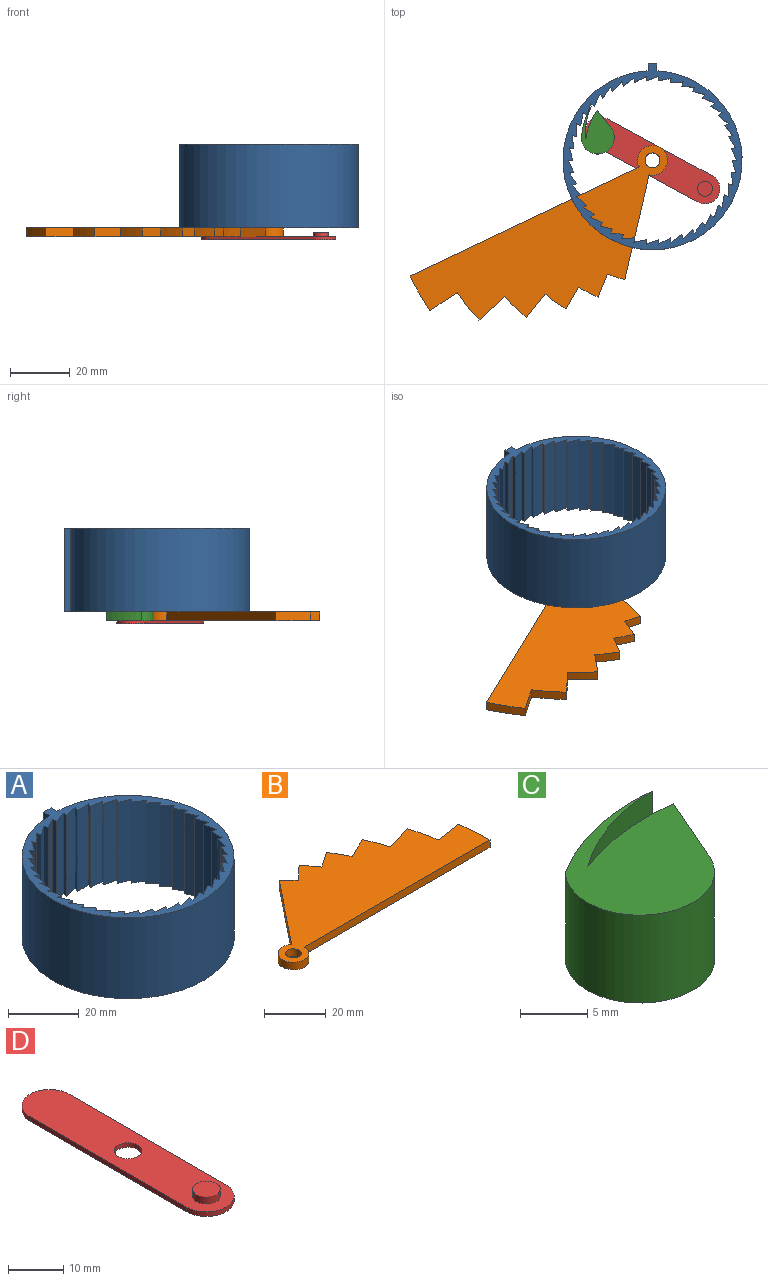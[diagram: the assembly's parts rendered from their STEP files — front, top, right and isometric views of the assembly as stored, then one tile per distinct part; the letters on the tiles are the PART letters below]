
ASSEMBLY  parts=4 mates=3
PART A: 90 faces, bbox 60x62.3x28 mm
  f0: plane 28x2.3mm, normal (-1,0,0), area 64.4mm2, adj f1,f87,f88,f89
  f1: cylinder r=30mm len=60mm, axis (0,0,-1), area 5193.8mm2, adj f0,f2,f88,f89
  f2: plane 28x2.3mm, normal (1,0,0), area 64.4mm2, adj f1,f87,f88,f89
  f3: plane 28x3.98mm, normal (-0.91,-0.41,0), area 122.2mm2, adj f4,f86,f88,f89
  f4: plane 28x1.5mm, normal (0,1,0), area 42mm2, adj f3,f5,f88,f89
  f5: plane 28x4.2mm, normal (-0.96,-0.27,0), area 122.2mm2, adj f4,f6,f88,f89
  f6: plane 28x1.48mm, normal (0.15,0.99,0), area 42mm2, adj f5,f7,f88,f89
  f7: plane 28x4.33mm, normal (-0.99,-0.13,0), area 122.2mm2, adj f6,f8,f88,f89
  f8: plane 28x1.43mm, normal (0.29,0.96,0), area 42mm2, adj f7,f9,f88,f89
  f9: plane 28x4.36mm, normal (-1,0.02,0), area 122.2mm2, adj f8,f10,f88,f89
  f10: plane 28x1.35mm, normal (0.43,0.9,0), area 42mm2, adj f9,f11,f88,f89
  f11: plane 28x4.3mm, normal (-0.98,0.17,0), area 122.2mm2, adj f10,f12,f88,f89
  f12: plane 28x1.24mm, normal (0.56,0.83,0), area 42mm2, adj f11,f13,f88,f89
  f13: plane 28x4.14mm, normal (-0.95,0.32,0), area 122.2mm2, adj f12,f14,f88,f89
  f14: plane 28x1.1mm, normal (0.68,0.73,0), area 42mm2, adj f13,f15,f88,f89
  f15: plane 28x3.89mm, normal (-0.89,0.46,0), area 122.2mm2, adj f14,f16,f88,f89
  f16: plane 28x1.17mm, normal (0.78,0.62,0), area 42mm2, adj f15,f17,f88,f89
  f17: plane 28x3.55mm, normal (-0.81,0.58,0), area 122.2mm2, adj f16,f18,f88,f89
  f18: plane 28x1.3mm, normal (0.87,0.5,0), area 42mm2, adj f17,f19,f88,f89
  f19: plane 28x3.13mm, normal (-0.72,0.7,0), area 122.2mm2, adj f18,f20,f88,f89
  f20: plane 28x1.4mm, normal (0.93,0.37,0), area 42mm2, adj f19,f21,f88,f89
  f21: plane 28x3.48mm, normal (-0.6,0.8,0), area 122.2mm2, adj f20,f22,f88,f89
  f22: plane 28x1.46mm, normal (0.97,0.22,0), area 42mm2, adj f21,f23,f88,f89
  f23: plane 28x3.83mm, normal (-0.48,0.88,0), area 122.2mm2, adj f22,f24,f88,f89
  f24: plane 28x1.5mm, normal (1,0.07,0), area 42mm2, adj f23,f25,f88,f89
  f25: plane 28x4.1mm, normal (-0.34,0.94,0), area 122.2mm2, adj f24,f26,f88,f89
  f26: plane 28x1.5mm, normal (1,-0.07,0), area 42mm2, adj f25,f27,f88,f89
  f27: plane 28x4.28mm, normal (-0.2,0.98,0), area 122.2mm2, adj f26,f28,f88,f89
  f28: plane 28x1.46mm, normal (0.97,-0.22,0), area 42mm2, adj f27,f29,f88,f89
  f29: plane 28x4.36mm, normal (-0.05,1,0), area 122.2mm2, adj f28,f30,f88,f89
  f30: plane 28x1.4mm, normal (0.93,-0.37,0), area 42mm2, adj f29,f31,f88,f89
  f31: plane 28x4.34mm, normal (0.1,1,0), area 122.2mm2, adj f30,f32,f88,f89
  f32: plane 28x1.3mm, normal (0.87,-0.5,0), area 42mm2, adj f31,f33,f88,f89
  f33: plane 28x4.23mm, normal (0.25,0.97,0), area 122.2mm2, adj f32,f34,f88,f89
  f34: plane 28x1.17mm, normal (0.78,-0.62,0), area 42mm2, adj f33,f35,f88,f89
  f35: plane 28x4.02mm, normal (0.39,0.92,0), area 122.2mm2, adj f34,f36,f88,f89
  f36: plane 28x1.1mm, normal (0.68,-0.73,0), area 42mm2, adj f35,f37,f88,f89
  f37: plane 28x3.73mm, normal (0.52,0.85,0), area 122.2mm2, adj f36,f38,f88,f89
  f38: plane 28x1.24mm, normal (0.56,-0.83,0), area 42mm2, adj f37,f39,f88,f89
  f39: plane 28x3.35mm, normal (0.64,0.77,0), area 122.2mm2, adj f38,f40,f88,f89
  f40: plane 28x1.35mm, normal (0.43,-0.9,0), area 42mm2, adj f39,f41,f88,f89
  f41: plane 28x3.27mm, normal (0.75,0.66,0), area 122.2mm2, adj f40,f42,f88,f89
  f42: plane 28x1.43mm, normal (0.29,-0.96,0), area 42mm2, adj f41,f43,f88,f89
  f43: plane 28x3.66mm, normal (0.84,0.54,0), area 122.2mm2, adj f42,f44,f88,f89
  f44: plane 28x1.48mm, normal (0.15,-0.99,0), area 42mm2, adj f43,f45,f88,f89
  f45: plane 28x3.98mm, normal (0.91,0.41,0), area 122.2mm2, adj f44,f46,f88,f89
  f46: plane 28x1.5mm, normal (0,-1,0), area 42mm2, adj f45,f47,f88,f89
  f47: plane 28x4.2mm, normal (0.96,0.27,0), area 122.2mm2, adj f46,f48,f88,f89
  f48: plane 28x1.48mm, normal (-0.15,-0.99,0), area 42mm2, adj f47,f49,f88,f89
  f49: plane 28x4.33mm, normal (0.99,0.13,0), area 122.2mm2, adj f48,f50,f88,f89
  f50: plane 28x1.43mm, normal (-0.29,-0.96,0), area 42mm2, adj f49,f51,f88,f89
  f51: plane 28x4.36mm, normal (1,-0.02,0), area 122.2mm2, adj f50,f52,f88,f89
  f52: plane 28x1.35mm, normal (-0.43,-0.9,0), area 42mm2, adj f51,f53,f88,f89
  f53: plane 28x4.3mm, normal (0.98,-0.17,0), area 122.2mm2, adj f52,f54,f88,f89
  f54: plane 28x1.24mm, normal (-0.56,-0.83,0), area 42mm2, adj f53,f55,f88,f89
  f55: plane 28x4.14mm, normal (0.95,-0.32,0), area 122.2mm2, adj f54,f56,f88,f89
  f56: plane 28x1.1mm, normal (-0.68,-0.73,0), area 42mm2, adj f55,f57,f88,f89
  f57: plane 28x3.89mm, normal (0.89,-0.46,0), area 122.2mm2, adj f56,f58,f88,f89
  f58: plane 28x1.17mm, normal (-0.78,-0.62,0), area 42mm2, adj f57,f59,f88,f89
  f59: plane 28x3.55mm, normal (0.81,-0.58,0), area 122.2mm2, adj f58,f60,f88,f89
  f60: plane 28x1.3mm, normal (-0.87,-0.5,0), area 42mm2, adj f59,f61,f88,f89
  f61: plane 28x3.13mm, normal (0.72,-0.7,0), area 122.2mm2, adj f60,f62,f88,f89
  f62: plane 28x1.4mm, normal (-0.93,-0.37,0), area 42mm2, adj f61,f63,f88,f89
  f63: plane 28x3.48mm, normal (0.6,-0.8,0), area 122.2mm2, adj f62,f64,f88,f89
  f64: plane 28x1.46mm, normal (-0.97,-0.22,0), area 42mm2, adj f63,f65,f88,f89
  f65: plane 28x3.83mm, normal (0.48,-0.88,0), area 122.2mm2, adj f64,f66,f88,f89
  f66: plane 28x1.5mm, normal (-1,-0.07,0), area 42mm2, adj f65,f67,f88,f89
  f67: plane 28x4.1mm, normal (0.34,-0.94,0), area 122.2mm2, adj f66,f68,f88,f89
  f68: plane 28x1.5mm, normal (-1,0.07,0), area 42mm2, adj f67,f69,f88,f89
  f69: plane 28x4.28mm, normal (0.2,-0.98,0), area 122.2mm2, adj f68,f70,f88,f89
  f70: plane 28x1.46mm, normal (-0.97,0.22,0), area 42mm2, adj f69,f71,f88,f89
  f71: plane 28x4.36mm, normal (0.05,-1,0), area 122.2mm2, adj f70,f72,f88,f89
  f72: plane 28x1.4mm, normal (-0.93,0.37,0), area 42mm2, adj f71,f73,f88,f89
  f73: plane 28x4.34mm, normal (-0.1,-1,0), area 122.2mm2, adj f72,f74,f88,f89
  f74: plane 28x1.3mm, normal (-0.87,0.5,0), area 42mm2, adj f73,f75,f88,f89
  f75: plane 28x4.23mm, normal (-0.25,-0.97,0), area 122.2mm2, adj f74,f76,f88,f89
  f76: plane 28x1.17mm, normal (-0.78,0.62,0), area 42mm2, adj f75,f77,f88,f89
  f77: plane 28x4.02mm, normal (-0.39,-0.92,0), area 122.2mm2, adj f76,f78,f88,f89
  f78: plane 28x1.1mm, normal (-0.68,0.73,0), area 42mm2, adj f77,f79,f88,f89
  f79: plane 28x3.73mm, normal (-0.52,-0.85,0), area 122.2mm2, adj f78,f80,f88,f89
  f80: plane 28x1.24mm, normal (-0.56,0.83,0), area 42mm2, adj f79,f81,f88,f89
  f81: plane 28x3.35mm, normal (-0.64,-0.77,0), area 122.2mm2, adj f80,f82,f88,f89
  f82: plane 28x1.35mm, normal (-0.43,0.9,0), area 42mm2, adj f81,f83,f88,f89
  f83: plane 28x3.27mm, normal (-0.75,-0.66,0), area 122.2mm2, adj f82,f84,f88,f89
  f84: plane 28x1.43mm, normal (-0.29,0.96,0), area 42mm2, adj f83,f85,f88,f89
  f85: plane 28x3.66mm, normal (-0.84,-0.54,0), area 122.2mm2, adj f84,f86,f88,f89
  f86: plane 28x1.48mm, normal (-0.15,0.99,0), area 42mm2, adj f3,f85,f88,f89
  f87: plane 28x3mm, normal (0,1,0), area 84mm2, adj f0,f2,f88,f89
  f88: plane 62.26x60mm, normal (0,0,1), area 481.1mm2, adj f0,f1,f2,f3,f4,f5,f6,f7
  f89: plane 62.26x60mm, normal (0,0,-1), area 481.1mm2, adj f0,f1,f2,f3,f4,f5,f6,f7
PART B: 17 faces, bbox 95x38.5x3 mm
  f0: plane 9.01x4.34mm, normal (-0.43,0.9,0), area 30mm2, adj f1,f13,f15,f16
  f1: cylinder r=57.5mm len=7.44mm, axis (0,0,-1), area 25.8mm2, adj f0,f2,f15,f16
  f2: plane 6.82x4.65mm, normal (-0.56,0.83,0), area 24.7mm2, adj f1,f3,f15,f16
  f3: cylinder r=49.25mm len=5.76mm, axis (0,0,-1), area 22.1mm2, adj f2,f4,f15,f16
  f4: plane 6.05x5.61mm, normal (-0.68,0.73,0), area 24.7mm2, adj f3,f5,f15,f16
  f5: cylinder r=41mm len=4.49mm, axis (0,0,-1), area 18.4mm2, adj f4,f6,f15,f16
  f6: plane 28.15x22.45mm, normal (-0.78,0.62,0), area 108mm2, adj f5,f7,f15,f16
  f7: cylinder r=5mm len=10mm, axis (0,0,-1), area 80.8mm2, adj f6,f8,f15,f16
  f8: plane 85x3mm, normal (0,-1,0), area 255mm2, adj f7,f9,f15,f16
  f9: cylinder r=90mm len=13.41mm, axis (0,0,-1), area 40.4mm2, adj f8,f10,f15,f16
  f10: plane 10.88x3mm, normal (-0.15,0.99,0), area 33mm2, adj f9,f11,f15,f16
  f11: cylinder r=79mm len=11.51mm, axis (0,0,-1), area 35.5mm2, adj f10,f12,f15,f16
  f12: plane 10.99x3.39mm, normal (-0.29,0.96,0), area 34.5mm2, adj f11,f13,f15,f16
  f13: cylinder r=67.5mm len=9.39mm, axis (0,0,-1), area 30.3mm2, adj f0,f12,f15,f16
  f14: cylinder r=2.5mm len=5mm, axis (0,0,-1), area 47.1mm2, adj f15,f16
  f15: plane 95x38.5mm, normal (0,0,1), area 2015.7mm2, adj f0,f1,f2,f3,f4,f5,f6,f7
  f16: plane 95x38.5mm, normal (0,0,-1), area 2015.7mm2, adj f0,f1,f2,f3,f4,f5,f6,f7
PART C: 8 faces, bbox 13.6x12.4x8 mm
  f0: plane 8x0.01mm, normal (0.07,1,0), area 0.1mm2, adj f4,f5,f6,f7
  f1: cylinder r=18.89mm len=11.89mm, axis (0,0,1), area 99.5mm2, adj f2,f5,f6,f7
  f2: cylinder r=5.54mm len=10.76mm, axis (0,0,1), area 159.5mm2, adj f1,f3,f6,f7
  f3: plane 8x6.36mm, normal (0.92,-0.4,0), area 55.4mm2, adj f2,f4,f6,f7
  f4: cylinder r=20.27mm len=10.22mm, axis (0,0,1), area 83.3mm2, adj f0,f3,f6,f7
  f5: cylinder r=17.59mm len=10.3mm, axis (0,0,1), area 88.5mm2, adj f0,f1,f6,f7
  f6: plane 13.57x12.4mm, normal (0,0,-1), area 107.3mm2, adj f0,f1,f2,f3,f4,f5
  f7: plane 13.57x12.4mm, normal (0,0,1), area 107.3mm2, adj f0,f1,f2,f3,f4,f5
PART D: 9 faces, bbox 10x50x2.5 mm
  f0: cylinder r=5mm len=10mm, axis (0,0,-1), area 15.7mm2, adj f1,f3,f5,f6
  f1: plane 40x1mm, normal (-1,0,0), area 40mm2, adj f0,f2,f5,f6
  f2: cylinder r=5mm len=10mm, axis (0,0,-1), area 15.7mm2, adj f1,f3,f5,f6
  f3: plane 40x1mm, normal (1,0,0), area 40mm2, adj f0,f2,f5,f6
  f4: cylinder r=2.5mm len=5mm, axis (0,0,-1), area 15.7mm2, adj f5,f6
  f5: plane 50x10mm, normal (0,0,1), area 439.3mm2, adj f0,f1,f2,f3,f4,f7
  f6: plane 50x10mm, normal (0,0,-1), area 458.9mm2, adj f0,f1,f2,f3,f4
  f7: cylinder r=2.5mm len=5mm, axis (0,0,-1), area 23.6mm2, adj f5,f8
  f8: plane 5x5mm, normal (0,0,1), area 19.6mm2, adj f7
PLACE A t=(76.71,18.98,-16.59)mm fixed
PLACE B rot(axis=(0,0,-1),154.5deg) t=(76.71,18.98,-19.59)mm
PLACE C rot(axis=(0,0,1),61.6deg) t=(75.93,17.13,-19.59)mm
PLACE D rot(axis=(0,0,1),61.6deg) t=(76.71,18.98,-20.09)mm
MATE revolute D.f4 <-> B.f7  axis (0,0,1) through (76.71,18.98,-19.59)mm
MATE revolute B.f14 <-> A.f1  axis (0,0,1) through (76.71,18.98,-16.59)mm
MATE fastened D.f0 <-> C.f6  axis (0,0,1) through (59.13,28.51,-19.59)mm
